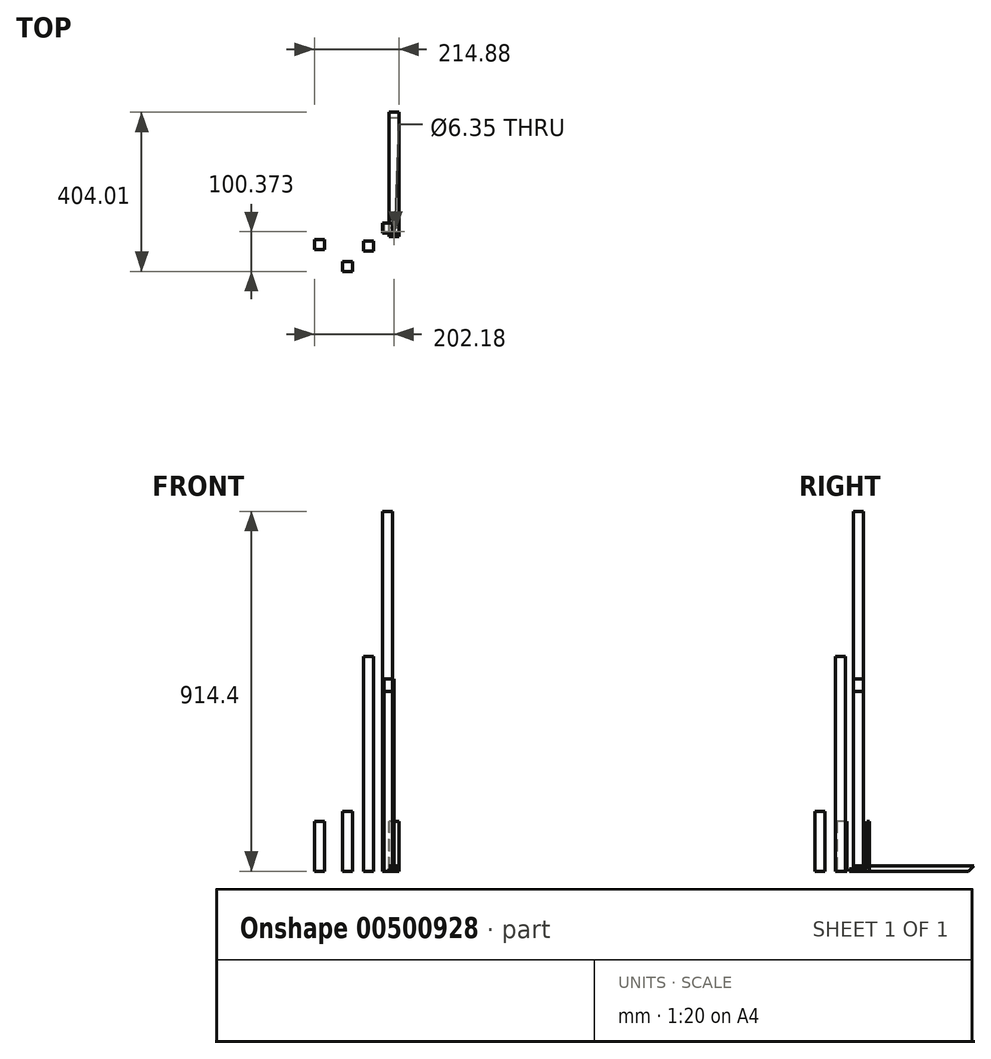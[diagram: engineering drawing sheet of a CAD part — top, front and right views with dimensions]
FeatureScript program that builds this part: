
annotation { "Feature Type Name" : "Feature", "Feature Type Description" : "" }
export const myFeature = defineFeature(function(context is Context, id is Id, definition is map)
    precondition{}
    {
        {
            var Q0;
            Q0=qCreatedBy(makeId("Top.planeOp"),FACE);
            var sketch = newSketch(context, id + "F0", { "sketchPlane" : qUnion([Q0])});
            skLineSegment(sketch, "E0.bottom", {"start": v(12.7, 12.7) * mm, "end": v(-12.7, 12.7) * mm});
            skLineSegment(sketch, "E0.top", {"start": v(12.7, -12.7) * mm, "end": v(-12.7, -12.7) * mm});
            skLineSegment(sketch, "E0.left", {"start": v(12.7, 12.7) * mm, "end": v(12.7, -12.7) * mm});
            skLineSegment(sketch, "E0.right", {"start": v(-12.7, 12.7) * mm, "end": v(-12.7, -12.7) * mm});
            skPoint(sketch, "E0.middle", {"position": v(0, 0) * mm});
            skSolve(sketch);
        }
        {
            var Q0;
            Q0=makeQuery(id+"F0.imprint","IMPRINT",FACE,{"disambiguationData":[TD([[makeQuery(id+"F0.imprint","IMPRINT",EDGE,{"derivedFrom":sQuery(id+"F0.wireOp",EDGE,"E0.bottom")}),1.0]])]});
            extrude(context, id + "F1", {"entities" : qUnion([Q0]), "depth" : 457.2 * mm});
        }
        {
            var Q0;
            Q0=qCreatedBy(makeId("Top.planeOp"),FACE);
            var sketch = newSketch(context, id + "F2", { "sketchPlane" : qUnion([Q0])});
            skLineSegment(sketch, "E1.bottom", {"start": v(-38.94, -33.07) * mm, "end": v(-64.34, -33.07) * mm});
            skLineSegment(sketch, "E1.top", {"start": v(-38.94, -58.47) * mm, "end": v(-64.34, -58.47) * mm});
            skLineSegment(sketch, "E1.left", {"start": v(-38.94, -33.07) * mm, "end": v(-38.94, -58.47) * mm});
            skLineSegment(sketch, "E1.right", {"start": v(-64.34, -33.07) * mm, "end": v(-64.34, -58.47) * mm});
            skPoint(sketch, "E1.middle", {"position": v(-51.64, -45.77) * mm});
            skSolve(sketch);
        }
        {
            var Q0;
            Q0 = qSketchRegion(id + "F2", true);
            extrude(context, id + "F3", {"entities" : qUnion([Q0]), "depth" : 546.1 * mm});
        }
        {
            var Q0;
            Q0=qCreatedBy(makeId("Right.planeOp"),FACE);
            var sketch = newSketch(context, id + "F4", { "sketchPlane" : qUnion([Q0])});
            skLineSegment(sketch, "E2", {"start": v(28.02, 0) * mm, "end": v(-22.78, 0) * mm});
            skLineSegment(sketch, "E3", {"start": v(-22.78, 0) * mm, "end": v(-22.78, 6.35) * mm});
            skLineSegment(sketch, "E4", {"start": v(-22.78, 6.35) * mm, "end": v(21.67, 6.35) * mm});
            skLineSegment(sketch, "E5", {"start": v(21.67, 6.35) * mm, "end": v(21.67, 127) * mm});
            skLineSegment(sketch, "E6", {"start": v(21.67, 127) * mm, "end": v(28.02, 127) * mm});
            skLineSegment(sketch, "E7", {"start": v(28.02, 127) * mm, "end": v(28.02, 0) * mm});
            skSolve(sketch);
        }
        {
            var Q0;
            Q0=makeQuery(id+"F4.imprint","IMPRINT",FACE,{"disambiguationData":[TD([[makeQuery(id+"F4.imprint","IMPRINT",EDGE,{"derivedFrom":sQuery(id+"F4.wireOp",EDGE,"E2")}),-1.0]])]});
            extrude(context, id + "F5", {"entities" : qUnion([Q0]), "depth" : 25.4 * mm});
        }
        {
            var Q0;
            Q0=qCreatedBy(makeId("Top.planeOp"),FACE);
            var sketch = newSketch(context, id + "F6", { "sketchPlane" : qUnion([Q0])});
            skLineSegment(sketch, "E8.bottom", {"start": v(-164.08, -29.51) * mm, "end": v(-189.48, -29.51) * mm});
            skLineSegment(sketch, "E8.top", {"start": v(-164.08, -54.91) * mm, "end": v(-189.48, -54.91) * mm});
            skLineSegment(sketch, "E8.left", {"start": v(-164.08, -29.51) * mm, "end": v(-164.08, -54.91) * mm});
            skLineSegment(sketch, "E8.right", {"start": v(-189.48, -29.51) * mm, "end": v(-189.48, -54.91) * mm});
            skPoint(sketch, "E8.middle", {"position": v(-176.78, -42.21) * mm});
            skSolve(sketch);
        }
        {
            var Q0;
            Q0 = qSketchRegion(id + "F6", true);
            extrude(context, id + "F7", {"entities" : qUnion([Q0]), "depth" : 127 * mm});
        }
        {
            var Q0;
            Q0=qCreatedBy(makeId("Top.planeOp"),FACE);
            var sketch = newSketch(context, id + "F8", { "sketchPlane" : qUnion([Q0])});
            skLineSegment(sketch, "E9.bottom", {"start": v(-118.1, -85.05) * mm, "end": v(-92.7, -85.05) * mm});
            skLineSegment(sketch, "E9.top", {"start": v(-118.1, -110.45) * mm, "end": v(-92.7, -110.45) * mm});
            skLineSegment(sketch, "E9.left", {"start": v(-118.1, -85.05) * mm, "end": v(-118.1, -110.45) * mm});
            skLineSegment(sketch, "E9.right", {"start": v(-92.7, -85.05) * mm, "end": v(-92.7, -110.45) * mm});
            skPoint(sketch, "E9.middle", {"position": v(-105.4, -97.75) * mm});
            skSolve(sketch);
        }
        {
            var Q0;
            Q0=makeQuery(id+"F8.imprint","IMPRINT",FACE,{"disambiguationData":[TD([[makeQuery(id+"F8.imprint","IMPRINT",EDGE,{"derivedFrom":sQuery(id+"F8.wireOp",EDGE,"E9.bottom")}),-1.0]])]});
            extrude(context, id + "F9", {"entities" : qUnion([Q0]), "depth" : 152.4 * mm});
        }
        {
            var Q0;
            Q0=qCreatedBy(makeId("Right.planeOp"),FACE);
            var sketch = newSketch(context, id + "F10", { "sketchPlane" : qUnion([Q0])});
            skLineSegment(sketch, "E10", {"start": v(0, 0) * mm, "end": v(279.4, 0) * mm});
            skLineSegment(sketch, "E11", {"start": v(279.4, 0) * mm, "end": v(293.56, 14.16) * mm});
            skLineSegment(sketch, "E12", {"start": v(293.56, 14.16) * mm, "end": v(-14.16, 14.16) * mm});
            skLineSegment(sketch, "E13", {"start": v(0, 0) * mm, "end": v(-14.16, 14.16) * mm});
            skSolve(sketch);
        }
        {
            var Q0;
            Q0=makeQuery(id+"F10.imprint","IMPRINT",FACE,{"disambiguationData":[TD([[makeQuery(id+"F10.imprint","IMPRINT",EDGE,{"derivedFrom":sQuery(id+"F10.wireOp",EDGE,"E10")}),1.0]])]});
            extrude(context, id + "F11", {"entities" : qUnion([Q0]), "depth" : 25.4 * mm});
        }
        {
            var Q0;
            Q0=qCreatedBy(makeId("Top.planeOp"),FACE);
            var sketch = newSketch(context, id + "F12", { "sketchPlane" : qUnion([Q0])});
            skLineSegment(sketch, "E14.bottom", {"start": v(9.02, 12.7) * mm, "end": v(-16.38, 12.7) * mm});
            skLineSegment(sketch, "E14.top", {"start": v(9.02, -12.7) * mm, "end": v(-16.38, -12.7) * mm});
            skLineSegment(sketch, "E14.left", {"start": v(9.02, 12.7) * mm, "end": v(9.02, -12.7) * mm});
            skLineSegment(sketch, "E14.right", {"start": v(-16.38, 12.7) * mm, "end": v(-16.38, -12.7) * mm});
            skPoint(sketch, "E14.middle", {"position": v(-3.68, 0) * mm});
            skSolve(sketch);
        }
        {
            var Q0;
            Q0=makeQuery(id+"F12.imprint","IMPRINT",FACE,{"disambiguationData":[TD([[makeQuery(id+"F12.imprint","IMPRINT",EDGE,{"derivedFrom":sQuery(id+"F12.wireOp",EDGE,"E14.bottom")}),1.0]])]});
            extrude(context, id + "F13", {"entities" : qUnion([Q0]), "depth" : 914.4 * mm});
        }
        {
            var Q0;
            Q0=qCreatedBy(makeId("Top.planeOp"),FACE);
            var sketch = newSketch(context, id + "F14", { "sketchPlane" : qUnion([Q0])});
            skLineSegment(sketch, "E15.bottom", {"start": v(12.7, 12.7) * mm, "end": v(-12.7, 12.7) * mm});
            skLineSegment(sketch, "E15.top", {"start": v(12.7, -12.7) * mm, "end": v(-12.7, -12.7) * mm});
            skLineSegment(sketch, "E15.left", {"start": v(12.7, 12.7) * mm, "end": v(12.7, -12.7) * mm});
            skLineSegment(sketch, "E15.right", {"start": v(-12.7, 12.7) * mm, "end": v(-12.7, -12.7) * mm});
            skPoint(sketch, "E15.middle", {"position": v(0, 0) * mm});
            skSolve(sketch);
        }
        {
            var Q0;
            Q0=makeQuery(id+"F14.imprint","IMPRINT",FACE,{"disambiguationData":[TD([[makeQuery(id+"F14.imprint","IMPRINT",EDGE,{"derivedFrom":sQuery(id+"F14.wireOp",EDGE,"E15.bottom")}),1.0]])]});
            extrude(context, id + "F15", {"entities" : qUnion([Q0]), "depth" : 488.95 * mm});
        }
        {
            var Q0;
            Q0=makeQuery(id+"F5.opExtrude","SWEPT_FACE",FACE,{"disambiguationData":[OSD([sQuery(id+"F4.wireOp",EDGE,"E4")])]});
            var sketch = newSketch(context, id + "F16", { "sketchPlane" : qUnion([Q0])});
            skCircle(sketch, "E16", {"center": v(12.7, -10.08) * mm, "radius": 3.18 * mm});
            skSolve(sketch);
        }
        {
            var Q0;
            Q0=sQuery(id+"F16.wireOp",VERTEX,"E16.center");
            var Q1;
            Q1=makeQuery(id+"F5.opExtrude","SWEPT_BODY",BODY,{"disambiguationData":[OSD([sQuery(id+"F4.wireOp",EDGE,"E2"),sQuery(id+"F4.wireOp",EDGE,"E3"),sQuery(id+"F4.wireOp",EDGE,"E4"),sQuery(id+"F4.wireOp",EDGE,"E5"),sQuery(id+"F4.wireOp",EDGE,"E6"),sQuery(id+"F4.wireOp",EDGE,"E7")])]});
            hole(context, id + "F17", {"style" : HoleStyle.SIMPLE, "endStyle" : HoleEndStyle.BLIND, "holeDiameter" : 6.35 * mm, "holeDepth" : 25.4 * mm, "isTappedThrough" : true, "tappedDepth" : 12.7 * mm, "tapClearance" : 3, "locations" : qUnion([Q0]), "scope" : qUnion([Q1]), "startStyle" : HoleStartStyle.PART});
        }
    });
